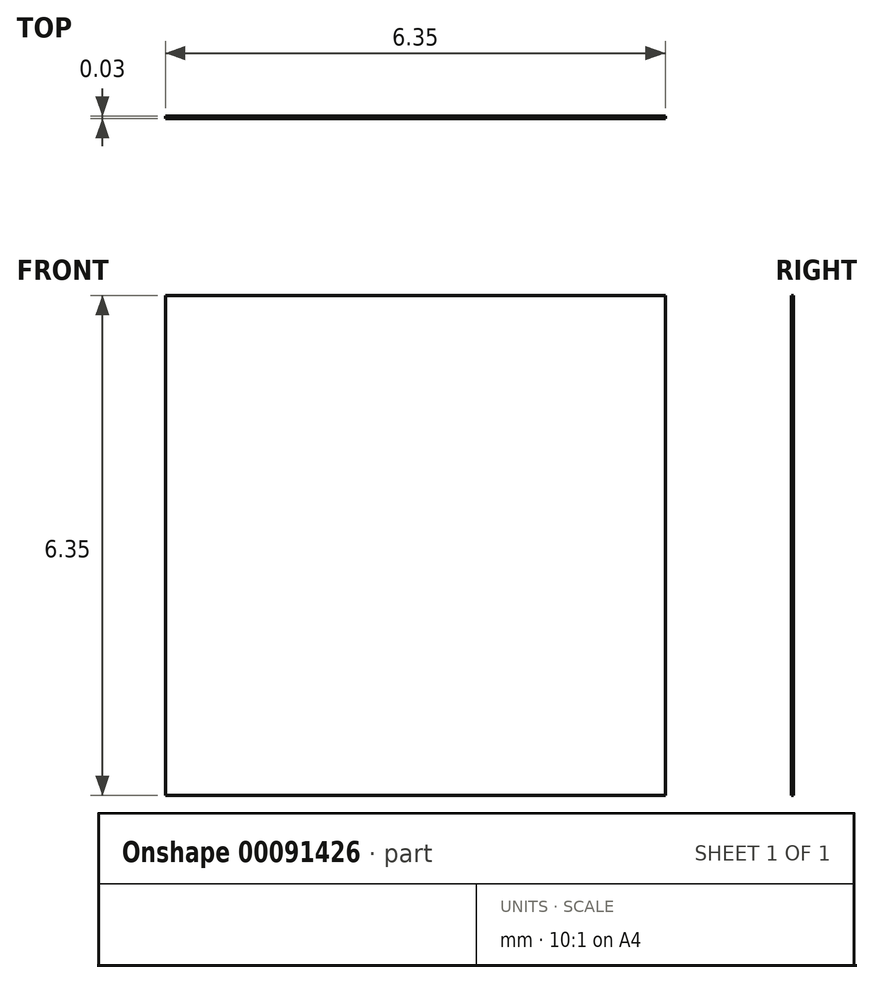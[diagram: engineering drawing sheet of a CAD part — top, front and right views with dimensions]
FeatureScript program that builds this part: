
annotation { "Feature Type Name" : "Feature", "Feature Type Description" : "" }
export const myFeature = defineFeature(function(context is Context, id is Id, definition is map)
    precondition{}
    {
        {
            var Q0;
            Q0=qCreatedBy(makeId("Front.planeOp"),FACE);
            var sketch = newSketch(context, id + "F0", { "sketchPlane" : qUnion([Q0])});
            skLineSegment(sketch, "E0.bottom", {"start": v(0, 0) * mm, "end": v(6.35, 0) * mm});
            skLineSegment(sketch, "E0.top", {"start": v(0, 6.35) * mm, "end": v(6.35, 6.35) * mm});
            skLineSegment(sketch, "E0.left", {"start": v(0, 0) * mm, "end": v(0, 6.35) * mm});
            skLineSegment(sketch, "E0.right", {"start": v(6.35, 0) * mm, "end": v(6.35, 6.35) * mm});
            skSolve(sketch);
        }
        {
            var Q0;
            Q0 = qSketchRegion(id + "F0", true);
            extrude(context, id + "F1", {"entities" : qUnion([Q0]), "depth" : 3 / 101.6 * mm});
        }
    });
